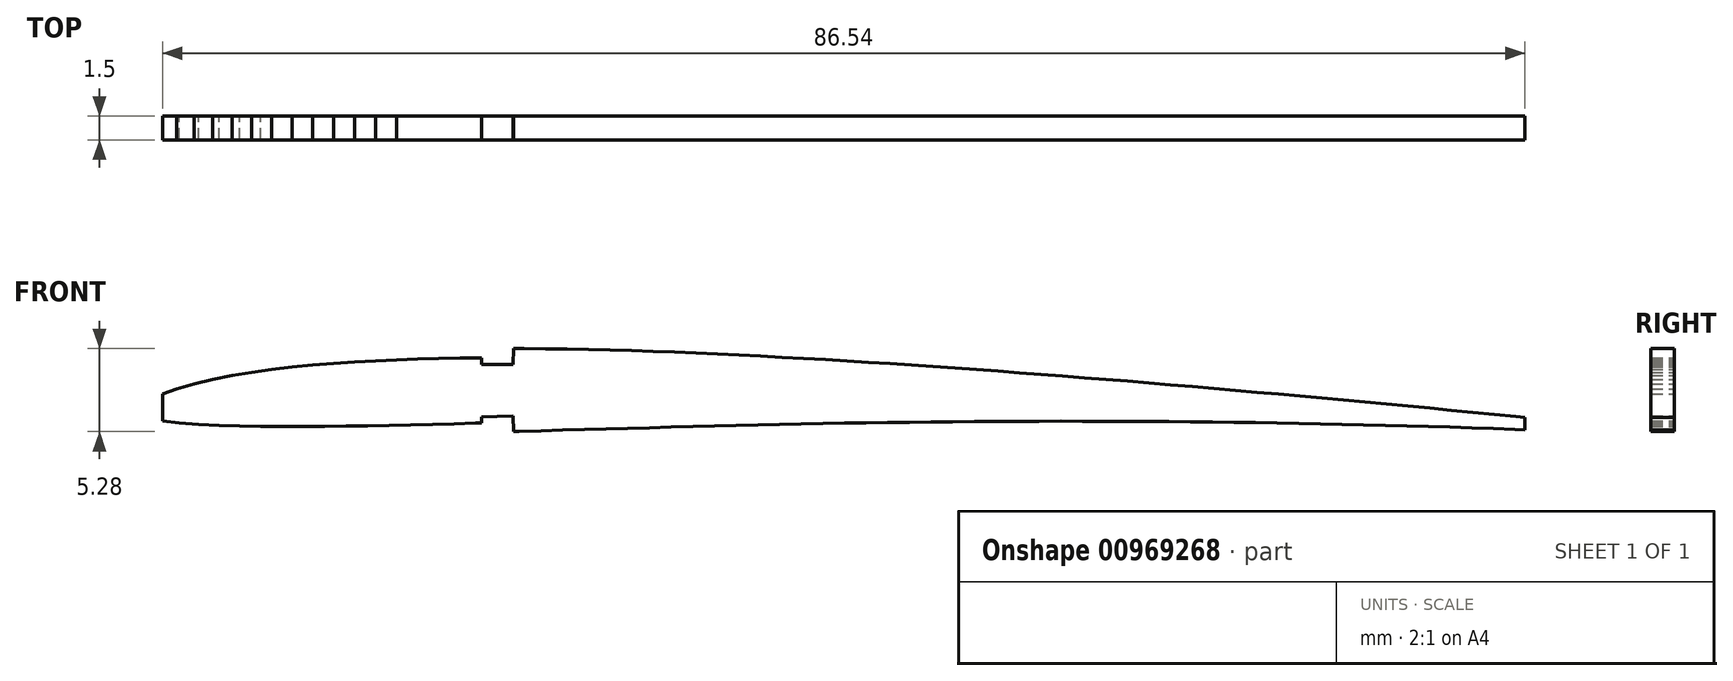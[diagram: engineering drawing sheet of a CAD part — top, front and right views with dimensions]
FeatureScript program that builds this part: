
annotation { "Feature Type Name" : "Feature", "Feature Type Description" : "" }
export const myFeature = defineFeature(function(context is Context, id is Id, definition is map)
    precondition{}
    {
        {
            var Q0;
            Q0=qCreatedBy(makeId("Front.planeOp"),FACE);
            var sketch = newSketch(context, id + "F0", { "sketchPlane" : qUnion([Q0])});
            skLineSegment(sketch, "E0", {"start": v(43.27, -2.52) * mm, "end": v(43.27, -1.74) * mm});
            skLineSegment(sketch, "E1", {"start": v(43.27, -1.74) * mm, "end": v(42.7, -1.68) * mm});
            skLineSegment(sketch, "E2", {"start": v(42.7, -1.68) * mm, "end": v(41.33, -1.55) * mm});
            skLineSegment(sketch, "E3", {"start": v(41.33, -1.55) * mm, "end": v(39.96, -1.42) * mm});
            skLineSegment(sketch, "E4", {"start": v(39.96, -1.42) * mm, "end": v(38.59, -1.28) * mm});
            skLineSegment(sketch, "E5", {"start": v(38.59, -1.28) * mm, "end": v(37.22, -1.15) * mm});
            skLineSegment(sketch, "E6", {"start": v(37.22, -1.15) * mm, "end": v(35.85, -1.02) * mm});
            skLineSegment(sketch, "E7", {"start": v(35.85, -1.02) * mm, "end": v(34.48, -0.9) * mm});
            skLineSegment(sketch, "E8", {"start": v(34.48, -0.9) * mm, "end": v(33.1, -0.76) * mm});
            skLineSegment(sketch, "E9", {"start": v(33.1, -0.76) * mm, "end": v(31.73, -0.64) * mm});
            skLineSegment(sketch, "E10", {"start": v(31.73, -0.64) * mm, "end": v(30.36, -0.51) * mm});
            skLineSegment(sketch, "E11", {"start": v(30.36, -0.51) * mm, "end": v(29, -0.39) * mm});
            skLineSegment(sketch, "E12", {"start": v(29, -0.39) * mm, "end": v(27.62, -0.26) * mm});
            skLineSegment(sketch, "E13", {"start": v(27.62, -0.26) * mm, "end": v(26.25, -0.14) * mm});
            skLineSegment(sketch, "E14", {"start": v(26.25, -0.14) * mm, "end": v(24.88, -0.02) * mm});
            skLineSegment(sketch, "E15", {"start": v(24.88, -0.02) * mm, "end": v(23.5, 0.1) * mm});
            skLineSegment(sketch, "E16", {"start": v(23.5, 0.1) * mm, "end": v(22.14, 0.22) * mm});
            skLineSegment(sketch, "E17", {"start": v(22.14, 0.22) * mm, "end": v(20.76, 0.33) * mm});
            skLineSegment(sketch, "E18", {"start": v(20.76, 0.33) * mm, "end": v(19.4, 0.45) * mm});
            skLineSegment(sketch, "E19", {"start": v(19.4, 0.45) * mm, "end": v(18.02, 0.56) * mm});
            skLineSegment(sketch, "E20", {"start": v(18.02, 0.56) * mm, "end": v(16.65, 0.67) * mm});
            skLineSegment(sketch, "E21", {"start": v(16.65, 0.67) * mm, "end": v(15.28, 0.78) * mm});
            skLineSegment(sketch, "E22", {"start": v(15.28, 0.78) * mm, "end": v(13.9, 0.9) * mm});
            skLineSegment(sketch, "E23", {"start": v(13.9, 0.9) * mm, "end": v(12.54, 1) * mm});
            skLineSegment(sketch, "E24", {"start": v(12.54, 1) * mm, "end": v(11.17, 1.1) * mm});
            skLineSegment(sketch, "E25", {"start": v(11.17, 1.1) * mm, "end": v(9.8, 1.2) * mm});
            skLineSegment(sketch, "E26", {"start": v(9.8, 1.2) * mm, "end": v(8.43, 1.3) * mm});
            skLineSegment(sketch, "E27", {"start": v(8.43, 1.3) * mm, "end": v(7.05, 1.4) * mm});
            skLineSegment(sketch, "E28", {"start": v(7.05, 1.4) * mm, "end": v(5.68, 1.5) * mm});
            skLineSegment(sketch, "E29", {"start": v(5.68, 1.5) * mm, "end": v(4.31, 1.59) * mm});
            skLineSegment(sketch, "E30", {"start": v(4.31, 1.59) * mm, "end": v(2.94, 1.68) * mm});
            skLineSegment(sketch, "E31", {"start": v(2.94, 1.68) * mm, "end": v(1.57, 1.76) * mm});
            skLineSegment(sketch, "E32", {"start": v(1.57, 1.76) * mm, "end": v(0.2, 1.85) * mm});
            skLineSegment(sketch, "E33", {"start": v(0.2, 1.85) * mm, "end": v(-1.17, 1.93) * mm});
            skLineSegment(sketch, "E34", {"start": v(-1.17, 1.93) * mm, "end": v(-2.54, 2) * mm});
            skLineSegment(sketch, "E35", {"start": v(-2.54, 2) * mm, "end": v(-3.9, 2.08) * mm});
            skLineSegment(sketch, "E36", {"start": v(-3.9, 2.08) * mm, "end": v(-5.28, 2.16) * mm});
            skLineSegment(sketch, "E37", {"start": v(-5.28, 2.16) * mm, "end": v(-6.65, 2.22) * mm});
            skLineSegment(sketch, "E38", {"start": v(-6.65, 2.22) * mm, "end": v(-8.02, 2.29) * mm});
            skLineSegment(sketch, "E39", {"start": v(-8.02, 2.29) * mm, "end": v(-9.38, 2.35) * mm});
            skLineSegment(sketch, "E40", {"start": v(-9.38, 2.35) * mm, "end": v(-10.75, 2.4) * mm});
            skLineSegment(sketch, "E41", {"start": v(-10.75, 2.4) * mm, "end": v(-12.12, 2.45) * mm});
            skLineSegment(sketch, "E42", {"start": v(-12.12, 2.45) * mm, "end": v(-13.49, 2.5) * mm});
            skLineSegment(sketch, "E43", {"start": v(-13.49, 2.5) * mm, "end": v(-14.85, 2.54) * mm});
            skLineSegment(sketch, "E44", {"start": v(-14.85, 2.54) * mm, "end": v(-16.22, 2.57) * mm});
            skLineSegment(sketch, "E45", {"start": v(-16.22, 2.57) * mm, "end": v(-17.58, 2.6) * mm});
            skLineSegment(sketch, "E46", {"start": v(-17.58, 2.6) * mm, "end": v(-18.94, 2.62) * mm});
            skLineSegment(sketch, "E47", {"start": v(-18.94, 2.62) * mm, "end": v(-20.3, 2.64) * mm});
            skLineSegment(sketch, "E48", {"start": v(-20.3, 2.64) * mm, "end": v(-20.98, 2.64) * mm});
            skLineSegment(sketch, "E49", {"start": v(-22.98, 2.04) * mm, "end": v(-23.02, 2.04) * mm});
            skLineSegment(sketch, "E50", {"start": v(-23.02, 2.04) * mm, "end": v(-24.37, 2.02) * mm});
            skLineSegment(sketch, "E51", {"start": v(-24.37, 2.02) * mm, "end": v(-25.72, 2) * mm});
            skLineSegment(sketch, "E52", {"start": v(-25.72, 2) * mm, "end": v(-27.06, 1.97) * mm});
            skLineSegment(sketch, "E53", {"start": v(-27.06, 1.97) * mm, "end": v(-28.4, 1.92) * mm});
            skLineSegment(sketch, "E54", {"start": v(-28.4, 1.92) * mm, "end": v(-29.74, 1.86) * mm});
            skLineSegment(sketch, "E55", {"start": v(-29.74, 1.86) * mm, "end": v(-31.08, 1.79) * mm});
            skLineSegment(sketch, "E56", {"start": v(-31.08, 1.79) * mm, "end": v(-32.4, 1.7) * mm});
            skLineSegment(sketch, "E57", {"start": v(-32.4, 1.7) * mm, "end": v(-33.72, 1.58) * mm});
            skLineSegment(sketch, "E58", {"start": v(-33.72, 1.58) * mm, "end": v(-35.03, 1.46) * mm});
            skLineSegment(sketch, "E59", {"start": v(-35.03, 1.46) * mm, "end": v(-36.32, 1.3) * mm});
            skLineSegment(sketch, "E60", {"start": v(-36.32, 1.3) * mm, "end": v(-37.6, 1.12) * mm});
            skLineSegment(sketch, "E61", {"start": v(-37.6, 1.12) * mm, "end": v(-38.85, 0.92) * mm});
            skLineSegment(sketch, "E62", {"start": v(-38.85, 0.92) * mm, "end": v(-40.07, 0.67) * mm});
            skLineSegment(sketch, "E63", {"start": v(-40.07, 0.67) * mm, "end": v(-41.25, 0.4) * mm});
            skLineSegment(sketch, "E64", {"start": v(-41.25, 0.4) * mm, "end": v(-42.36, 0.07) * mm});
            skLineSegment(sketch, "E65", {"start": v(-42.36, 0.07) * mm, "end": v(-43.27, -0.26) * mm});
            skLineSegment(sketch, "E66", {"start": v(-43.27, -1.97) * mm, "end": v(-43.27, -0.26) * mm});
            skLineSegment(sketch, "E67", {"start": v(-22.98, 2.04) * mm, "end": v(-22.98, 1.64) * mm});
            skLineSegment(sketch, "E68", {"start": v(-20.58, 2.64) * mm, "end": v(-20.58, 2.64) * mm});
            skLineSegment(sketch, "E69", {"start": v(-20.99, 1.64) * mm, "end": v(-21.66, 1.64) * mm});
            skLineSegment(sketch, "E70", {"start": v(-21.66, 1.64) * mm, "end": v(-22.98, 1.64) * mm});
            skLineSegment(sketch, "E71", {"start": v(-22.98, -1.7) * mm, "end": v(-22.98, -2.1) * mm});
            skLineSegment(sketch, "E72", {"start": v(-22.98, -1.7) * mm, "end": v(-22.01, -1.67) * mm});
            skLineSegment(sketch, "E73", {"start": v(-22.01, -1.67) * mm, "end": v(-21, -1.64) * mm});
            skLineSegment(sketch, "E74", {"start": v(-20.99, 1.64) * mm, "end": v(-20.98, 2.64) * mm});
            skLineSegment(sketch, "E75", {"start": v(-21, -1.64) * mm, "end": v(-20.97, -2.64) * mm});
            skLineSegment(sketch, "E76", {"start": v(-20.97, -2.64) * mm, "end": v(-20.6, -2.63) * mm});
            skLineSegment(sketch, "E77", {"start": v(-20.6, -2.63) * mm, "end": v(-19.23, -2.59) * mm});
            skLineSegment(sketch, "E78", {"start": v(-19.23, -2.59) * mm, "end": v(-17.85, -2.55) * mm});
            skLineSegment(sketch, "E79", {"start": v(-17.85, -2.55) * mm, "end": v(-16.47, -2.5) * mm});
            skLineSegment(sketch, "E80", {"start": v(-16.47, -2.5) * mm, "end": v(-15.1, -2.47) * mm});
            skLineSegment(sketch, "E81", {"start": v(-15.1, -2.47) * mm, "end": v(-13.71, -2.43) * mm});
            skLineSegment(sketch, "E82", {"start": v(-13.71, -2.43) * mm, "end": v(-12.34, -2.4) * mm});
            skLineSegment(sketch, "E83", {"start": v(-12.34, -2.4) * mm, "end": v(-10.96, -2.36) * mm});
            skLineSegment(sketch, "E84", {"start": v(-10.96, -2.36) * mm, "end": v(-9.58, -2.32) * mm});
            skLineSegment(sketch, "E85", {"start": v(-9.58, -2.32) * mm, "end": v(-8.2, -2.28) * mm});
            skLineSegment(sketch, "E86", {"start": v(-8.2, -2.28) * mm, "end": v(-6.83, -2.25) * mm});
            skLineSegment(sketch, "E87", {"start": v(-6.83, -2.25) * mm, "end": v(-5.45, -2.22) * mm});
            skLineSegment(sketch, "E88", {"start": v(-5.45, -2.22) * mm, "end": v(-4.08, -2.19) * mm});
            skLineSegment(sketch, "E89", {"start": v(-4.08, -2.19) * mm, "end": v(-2.7, -2.16) * mm});
            skLineSegment(sketch, "E90", {"start": v(-2.7, -2.16) * mm, "end": v(-1.33, -2.13) * mm});
            skLineSegment(sketch, "E91", {"start": v(-1.33, -2.13) * mm, "end": v(0.05, -2.1) * mm});
            skLineSegment(sketch, "E92", {"start": v(0.05, -2.1) * mm, "end": v(1.42, -2.08) * mm});
            skLineSegment(sketch, "E93", {"start": v(1.42, -2.08) * mm, "end": v(2.8, -2.06) * mm});
            skLineSegment(sketch, "E94", {"start": v(2.8, -2.06) * mm, "end": v(4.17, -2.04) * mm});
            skLineSegment(sketch, "E95", {"start": v(4.17, -2.04) * mm, "end": v(5.54, -2.03) * mm});
            skLineSegment(sketch, "E96", {"start": v(5.54, -2.03) * mm, "end": v(6.92, -2.01) * mm});
            skLineSegment(sketch, "E97", {"start": v(6.92, -2.01) * mm, "end": v(8.3, -2) * mm});
            skLineSegment(sketch, "E98", {"start": v(8.3, -2) * mm, "end": v(9.66, -2) * mm});
            skLineSegment(sketch, "E99", {"start": v(9.66, -2) * mm, "end": v(11.04, -1.98) * mm});
            skLineSegment(sketch, "E100", {"start": v(11.04, -1.98) * mm, "end": v(12.41, -1.98) * mm});
            skLineSegment(sketch, "E101", {"start": v(12.41, -1.98) * mm, "end": v(13.79, -1.98) * mm});
            skLineSegment(sketch, "E102", {"start": v(13.79, -1.98) * mm, "end": v(15.16, -1.98) * mm});
            skLineSegment(sketch, "E103", {"start": v(15.16, -1.98) * mm, "end": v(16.53, -1.98) * mm});
            skLineSegment(sketch, "E104", {"start": v(16.53, -1.98) * mm, "end": v(17.9, -1.99) * mm});
            skLineSegment(sketch, "E105", {"start": v(17.9, -1.99) * mm, "end": v(19.28, -2) * mm});
            skLineSegment(sketch, "E106", {"start": v(19.28, -2) * mm, "end": v(20.66, -2) * mm});
            skLineSegment(sketch, "E107", {"start": v(20.66, -2) * mm, "end": v(22.03, -2.02) * mm});
            skLineSegment(sketch, "E108", {"start": v(22.03, -2.02) * mm, "end": v(23.4, -2.03) * mm});
            skLineSegment(sketch, "E109", {"start": v(23.4, -2.03) * mm, "end": v(24.78, -2.05) * mm});
            skLineSegment(sketch, "E110", {"start": v(24.78, -2.05) * mm, "end": v(26.15, -2.07) * mm});
            skLineSegment(sketch, "E111", {"start": v(26.15, -2.07) * mm, "end": v(27.53, -2.1) * mm});
            skLineSegment(sketch, "E112", {"start": v(27.53, -2.1) * mm, "end": v(28.9, -2.12) * mm});
            skLineSegment(sketch, "E113", {"start": v(28.9, -2.12) * mm, "end": v(30.27, -2.14) * mm});
            skLineSegment(sketch, "E114", {"start": v(30.27, -2.14) * mm, "end": v(31.65, -2.17) * mm});
            skLineSegment(sketch, "E115", {"start": v(31.65, -2.17) * mm, "end": v(33.02, -2.2) * mm});
            skLineSegment(sketch, "E116", {"start": v(33.02, -2.2) * mm, "end": v(34.4, -2.24) * mm});
            skLineSegment(sketch, "E117", {"start": v(34.4, -2.24) * mm, "end": v(35.77, -2.28) * mm});
            skLineSegment(sketch, "E118", {"start": v(35.77, -2.28) * mm, "end": v(37.14, -2.31) * mm});
            skLineSegment(sketch, "E119", {"start": v(37.14, -2.31) * mm, "end": v(38.51, -2.36) * mm});
            skLineSegment(sketch, "E120", {"start": v(38.51, -2.36) * mm, "end": v(39.89, -2.4) * mm});
            skLineSegment(sketch, "E121", {"start": v(39.89, -2.4) * mm, "end": v(41.26, -2.45) * mm});
            skLineSegment(sketch, "E122", {"start": v(41.26, -2.45) * mm, "end": v(42.63, -2.5) * mm});
            skLineSegment(sketch, "E123", {"start": v(42.63, -2.5) * mm, "end": v(43.27, -2.52) * mm});
            skLineSegment(sketch, "E124", {"start": v(-43.27, -1.97) * mm, "end": v(-42.22, -2.1) * mm});
            skLineSegment(sketch, "E125", {"start": v(-42.22, -2.1) * mm, "end": v(-40.97, -2.18) * mm});
            skLineSegment(sketch, "E126", {"start": v(-40.97, -2.18) * mm, "end": v(-39.68, -2.25) * mm});
            skLineSegment(sketch, "E127", {"start": v(-39.68, -2.25) * mm, "end": v(-38.36, -2.28) * mm});
            skLineSegment(sketch, "E128", {"start": v(-38.36, -2.28) * mm, "end": v(-37.02, -2.3) * mm});
            skLineSegment(sketch, "E129", {"start": v(-37.02, -2.3) * mm, "end": v(-35.68, -2.32) * mm});
            skLineSegment(sketch, "E130", {"start": v(-35.68, -2.32) * mm, "end": v(-34.32, -2.31) * mm});
            skLineSegment(sketch, "E131", {"start": v(-34.32, -2.31) * mm, "end": v(-32.97, -2.3) * mm});
            skLineSegment(sketch, "E132", {"start": v(-32.97, -2.3) * mm, "end": v(-31.6, -2.29) * mm});
            skLineSegment(sketch, "E133", {"start": v(-31.6, -2.29) * mm, "end": v(-30.24, -2.27) * mm});
            skLineSegment(sketch, "E134", {"start": v(-30.24, -2.27) * mm, "end": v(-28.87, -2.24) * mm});
            skLineSegment(sketch, "E135", {"start": v(-28.87, -2.24) * mm, "end": v(-27.5, -2.2) * mm});
            skLineSegment(sketch, "E136", {"start": v(-27.5, -2.2) * mm, "end": v(-26.13, -2.18) * mm});
            skLineSegment(sketch, "E137", {"start": v(-26.13, -2.18) * mm, "end": v(-24.75, -2.14) * mm});
            skLineSegment(sketch, "E138", {"start": v(-24.75, -2.14) * mm, "end": v(-23.38, -2.1) * mm});
            skLineSegment(sketch, "E139", {"start": v(-23.38, -2.1) * mm, "end": v(-22.98, -2.1) * mm});
            skSolve(sketch);
        }
        {
            var Q0;
            Q0 = qSketchRegion(id + "F0", true);
            extrude(context, id + "F1", {"entities" : qUnion([Q0]), "depth" : 1.5 * mm, "offsetDistance" : 25 * mm});
        }
    });
